# Revit family: Brownbuilt 406 Apex Bullnose Family
name_source: partatom
category: Generic Models
revit_build: Autodesk Revit 2018 (Build: 20181011_1500(x64)
units: mm (PartAtom-declared; Revit-internal decimal feet)

## family parameters
Always vertical = Yes
Can host rebar = No
Cut with Voids When Loaded = No
Part Type = Normal
Room Calculation Point = No
Round Connector Dimension = Use Diameter
Shared = No
Work Plane-Based = No

## types (1)
- Brownbuilt 406 Apex Bullnose
    Adjustable length = 495 mm  [stored 1.62402 ft]
    Arc length = 686.61 mm
    Bullnose End = 75 mm
    Calculated length = 502.64 mm
    Calculated x value = 78.14 mm
    Calculated y value = 443.16 mm
    Disclaimer = Although care has been taken to ensure, to the best of our
knowledge, that all data and information contained herein
is accurate to the extent that it relates to either matters
of fact or accepted practice at the time of issue. GRS
assumes no responsibility for any errors in, or 
misinterpretation of, such data and/ or information or any
loss or damage arising from, or related to it's use.
    Inside radius = 450 mm  [stored 1.47638 ft]
    Manufacturer = Global Roofing Solutions
    Material = ISQ 300, Galvanized Z275
    Material Thickness = 0.58 mm  [stored 0.00190289 ft]
    Model = Brownbuilt 406 Apex Bullnose
    Outside radius = 492 mm  [stored 1.61417 ft]
    Roof Pitch = 10.00°
    Sheet length = 1264.25 mm
    Telephone = 011 898 2900
    URL = www.globalroof.co.za
    opposite = 80.00°

note: [stored X ft] marks values corroborated as IEEE doubles in the binary element streams (Revit-internal decimal feet)

## geometry (parser evidence)
native form markers: Sweep x4
no freeform markers — native parametric forms only
